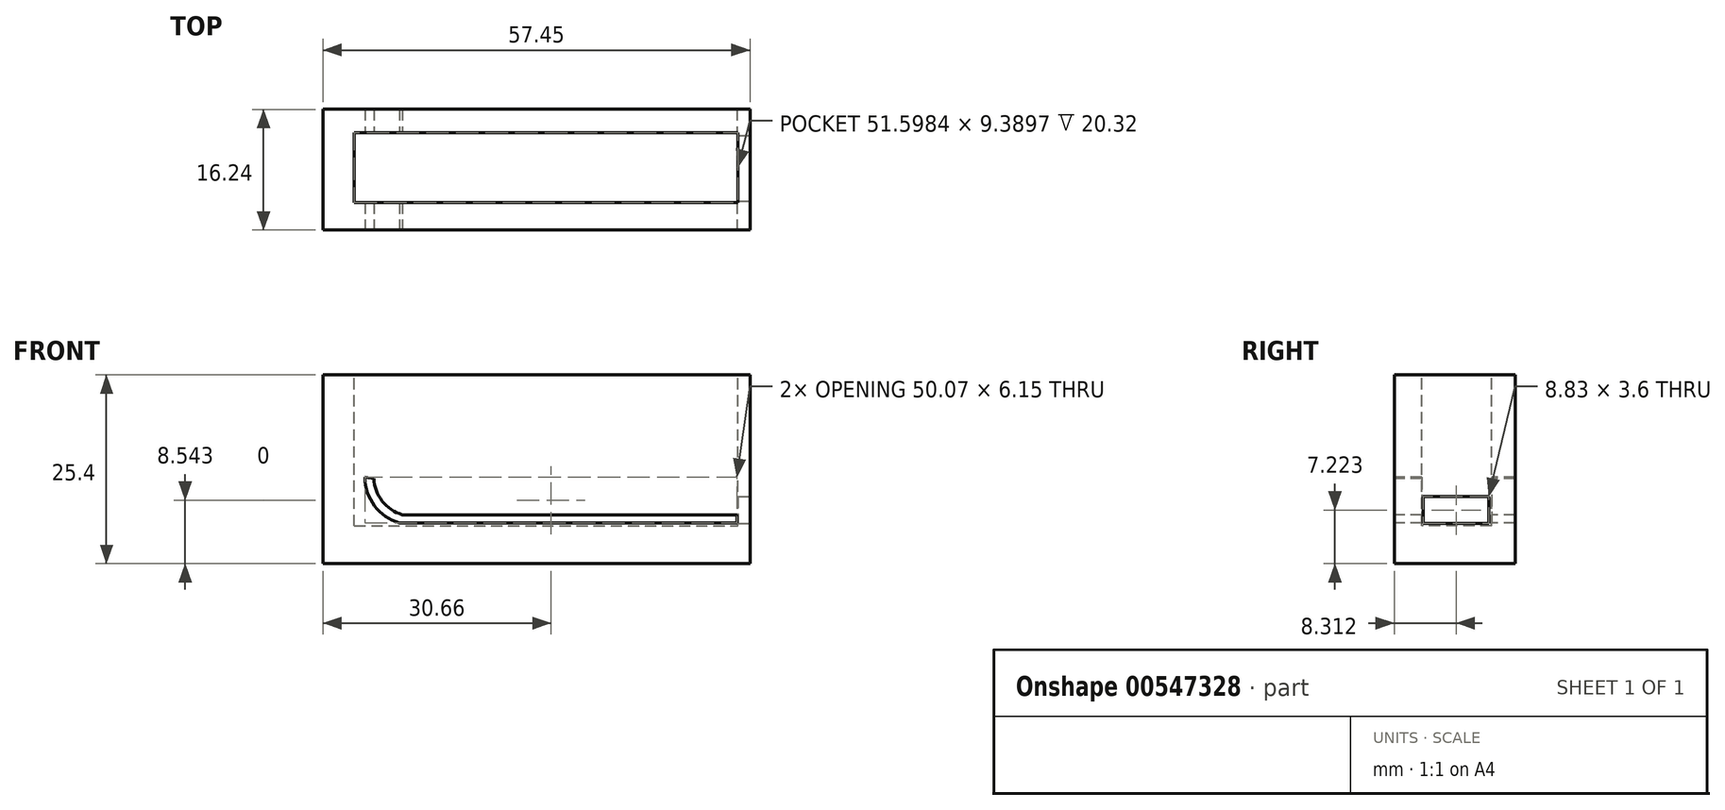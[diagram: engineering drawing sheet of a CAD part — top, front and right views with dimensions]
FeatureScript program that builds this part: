
annotation { "Feature Type Name" : "Feature", "Feature Type Description" : "" }
export const myFeature = defineFeature(function(context is Context, id is Id, definition is map)
    precondition{}
    {
        {
            var Q0;
            Q0=qCreatedBy(makeId("Top.planeOp"),FACE);
            var sketch = newSketch(context, id + "F0", { "sketchPlane" : qUnion([Q0])});
            skLineSegment(sketch, "E0.bottom", {"start": v(-28.88, 7.82) * mm, "end": v(28.57, 7.82) * mm});
            skLineSegment(sketch, "E0.top", {"start": v(-28.88, -8.42) * mm, "end": v(28.57, -8.42) * mm});
            skLineSegment(sketch, "E0.left", {"start": v(-28.88, 7.82) * mm, "end": v(-28.88, -8.42) * mm});
            skLineSegment(sketch, "E0.right", {"start": v(28.57, 7.82) * mm, "end": v(28.57, -8.42) * mm});
            skSolve(sketch);
        }
        {
            var Q0;
            Q0=makeQuery(id+"F0.imprint","IMPRINT",FACE,{"disambiguationData":[TD([[makeQuery(id+"F0.imprint","IMPRINT",EDGE,{"derivedFrom":sQuery(id+"F0.wireOp",EDGE,"E0.bottom")}),-1.0]])]});
            extrude(context, id + "F1", {"entities" : qUnion([Q0]), "depth" : 25.4 * mm, "offsetDistance" : 25.4 * mm});
        }
        {
            var Q0;
            Q0=makeQuery(id+"F1.opExtrude","CAP_FACE",FACE,{"disambiguationData":[OSD([sQuery(id+"F0.wireOp",EDGE,"E0.bottom"),sQuery(id+"F0.wireOp",EDGE,"E0.top"),sQuery(id+"F0.wireOp",EDGE,"E0.left"),sQuery(id+"F0.wireOp",EDGE,"E0.right")])],"isStart":false});
            var sketch = newSketch(context, id + "F2", { "sketchPlane" : qUnion([Q0])});
            skLineSegment(sketch, "E1.bottom", {"start": v(-24.67, 4.66) * mm, "end": v(26.93, 4.66) * mm});
            skLineSegment(sketch, "E1.top", {"start": v(-24.67, -4.73) * mm, "end": v(26.93, -4.73) * mm});
            skLineSegment(sketch, "E1.left", {"start": v(-24.67, 4.66) * mm, "end": v(-24.67, -4.73) * mm});
            skLineSegment(sketch, "E1.right", {"start": v(26.93, 4.66) * mm, "end": v(26.93, -4.73) * mm});
            skSolve(sketch);
        }
        {
            var Q0;
            Q0=makeQuery(id+"F2.imprint","IMPRINT",FACE,{"disambiguationData":[TD([[makeQuery(id+"F2.imprint","IMPRINT",EDGE,{"derivedFrom":sQuery(id+"F2.wireOp",EDGE,"E1.bottom")}),-1.0]])]});
            extrude(context, id + "F3", {"entities" : qUnion([Q0]), "operationType" : NewBodyOperationType.REMOVE, "oppositeDirection" : true, "depth" : 20.32 * mm, "offsetDistance" : 25.4 * mm});
        }
        {
            var Q0;
            Q0=makeQuery(id+"F1.opExtrude","SWEPT_FACE",FACE,{"disambiguationData":[OSD([sQuery(id+"F0.wireOp",EDGE,"E0.right")])]});
            var sketch = newSketch(context, id + "F4", { "sketchPlane" : qUnion([Q0])});
            skLineSegment(sketch, "E2.bottom", {"start": v(-4.52, 5.42) * mm, "end": v(4.3, 5.42) * mm});
            skLineSegment(sketch, "E2.top", {"start": v(-4.52, 9.02) * mm, "end": v(4.3, 9.02) * mm});
            skLineSegment(sketch, "E2.left", {"start": v(-4.52, 5.42) * mm, "end": v(-4.52, 9.02) * mm});
            skLineSegment(sketch, "E2.right", {"start": v(4.3, 5.42) * mm, "end": v(4.3, 9.02) * mm});
            skSolve(sketch);
        }
        {
            var Q0;
            Q0=makeQuery(id+"F4.imprint","IMPRINT",FACE,{"disambiguationData":[TD([[makeQuery(id+"F4.imprint","IMPRINT",EDGE,{"derivedFrom":sQuery(id+"F4.wireOp",EDGE,"E2.bottom")}),1.0]])]});
            extrude(context, id + "F5", {"entities" : qUnion([Q0]), "operationType" : NewBodyOperationType.REMOVE, "oppositeDirection" : true, "depth" : 35.3 * mm, "offsetDistance" : 25.4 * mm});
        }
        {
            var Q0;
            Q0=makeQuery(id+"F1.opExtrude","SWEPT_FACE",FACE,{"disambiguationData":[OSD([sQuery(id+"F0.wireOp",EDGE,"E0.top")])]});
            var sketch = newSketch(context, id + "F6", { "sketchPlane" : qUnion([Q0])});
            skLineSegment(sketch, "E3", {"start": v(26.79, 5.47) * mm, "end": v(-18.63, 5.47) * mm});
            skArc(sketch, "E4", {"start": v(-22.06, 11.48) * mm, "mid": v(-20.92, 8.42) * mm, "end": v(-18.22, 6.6) * mm});
            skLineSegment(sketch, "E5", {"start": v(-18.22, 6.6) * mm, "end": v(26.82, 6.6) * mm});
            skLineSegment(sketch, "E6", {"start": v(26.82, 6.6) * mm, "end": v(26.79, 5.47) * mm});
            skArc(sketch, "E7.0", {"start": v(-23.25, 11.62) * mm, "mid": v(-21.94, 7.79) * mm, "end": v(-18.63, 5.47) * mm});
            skLineSegment(sketch, "E8", {"start": v(-23.25, 11.62) * mm, "end": v(-22.06, 11.48) * mm});
            skSolve(sketch);
        }
        {
            var Q0;
            Q0 = qSketchRegion(id + "F6", true);
            extrude(context, id + "F7", {"entities" : qUnion([Q0]), "operationType" : NewBodyOperationType.REMOVE, "oppositeDirection" : true, "depth" : 25.4 * mm, "offsetDistance" : 25.4 * mm});
        }
    });
